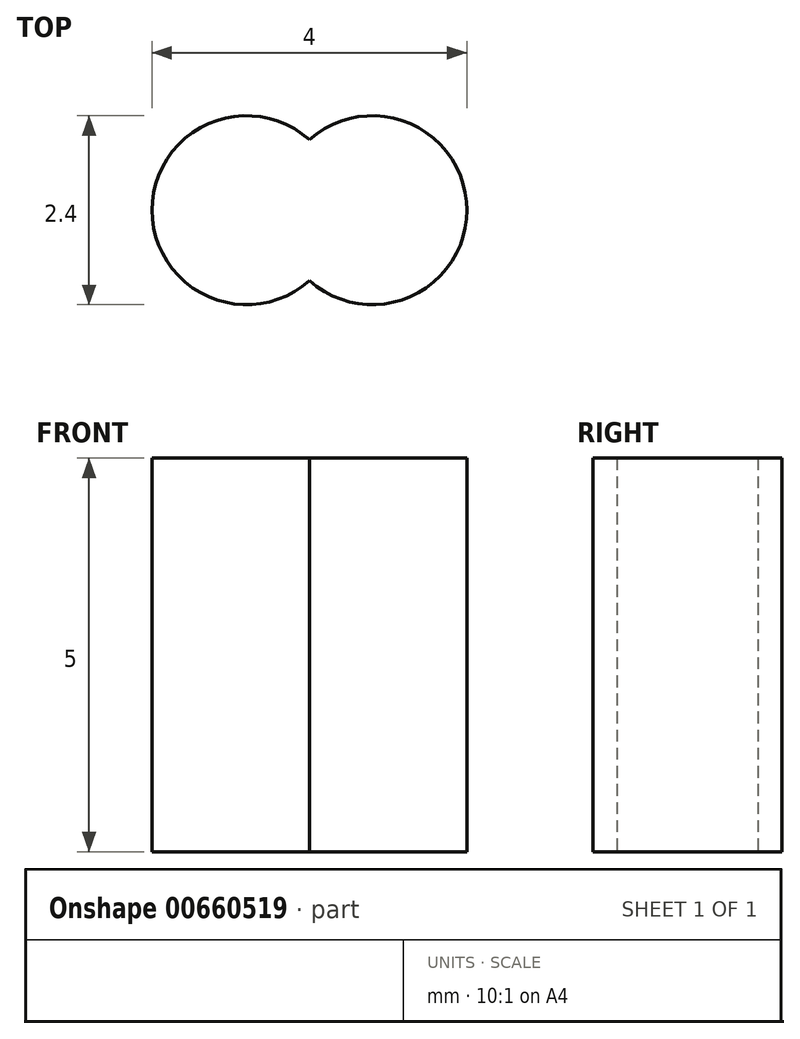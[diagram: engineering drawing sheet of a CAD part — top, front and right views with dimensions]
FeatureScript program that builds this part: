
annotation { "Feature Type Name" : "Feature", "Feature Type Description" : "" }
export const myFeature = defineFeature(function(context is Context, id is Id, definition is map)
    precondition{}
    {
        {
            var Q0;
            Q0=qCreatedBy(makeId("Top.planeOp"),FACE);
            var sketch = newSketch(context, id + "F0", { "sketchPlane" : qUnion([Q0])});
            skCircle(sketch, "E0", {"center": v(0, 0) * mm, "radius": 2 * mm});
            skCircle(sketch, "E1", {"center": v(-0.8, 0) * mm, "radius": 1.2 * mm});
            skCircle(sketch, "E2", {"center": v(0.8, 0) * mm, "radius": 1.2 * mm});
            skSolve(sketch);
        }
        {
            var Q0;
            {var subQ0=sQuery(id+"F0.wireOp",EDGE,"E1");var subQ1=makeQuery(id+"F0.imprint","INTERSECT",VERTEX,{"derivedFrom":[sQuery(id+"F0.wireOp",EDGE,"E0"),subQ0]});Q0=makeQuery(id+"F0.imprint","IMPRINT",FACE,{"disambiguationData":[TD([[makeQuery(id+"F0.imprint","IMPRINT",EDGE,{"disambiguationData":[TD([[subQ1,1.0]])],"derivedFrom":subQ0}),1.0]])]});}
            var Q1;
            {var subQ0=sQuery(id+"F0.wireOp",EDGE,"E2");var subQ1=sQuery(id+"F0.wireOp",EDGE,"E1");var subQ2=makeQuery(id+"F0.imprint","INTERSECT",VERTEX,{"disambiguationData":[OD(0.0)],"derivedFrom":[subQ1,subQ0]});Q1=makeQuery(id+"F0.imprint","IMPRINT",FACE,{"disambiguationData":[TD([[makeQuery(id+"F0.imprint","IMPRINT",EDGE,{"disambiguationData":[TD([[subQ2,1.0]])],"derivedFrom":subQ1}),-1.0]])]});}
            var Q2;
            {var subQ0=sQuery(id+"F0.wireOp",EDGE,"E2");var subQ1=sQuery(id+"F0.wireOp",EDGE,"E1");var subQ2=makeQuery(id+"F0.imprint","INTERSECT",VERTEX,{"disambiguationData":[OD(0.0)],"derivedFrom":[subQ1,subQ0]});Q2=makeQuery(id+"F0.imprint","IMPRINT",FACE,{"disambiguationData":[TD([[makeQuery(id+"F0.imprint","IMPRINT",EDGE,{"disambiguationData":[TD([[subQ2,1.0]])],"derivedFrom":subQ1}),1.0]])]});}
            extrude(context, id + "F1", {"entities" : qUnion([Q0, Q1, Q2]), "depth" : 5 * mm, "offsetDistance" : 25 * mm});
        }
    });
